# Revit family: QF_BOURGEAT_plaque_chauffante_classic_inox_600x400
name_source: partatom
category: Equipement spécialisé
revit_build: Autodesk Revit 2015 (Build: 20140606_1530(x64)
units: mm (PartAtom-declared; Revit-internal decimal feet)

## types (2) — shared parameters
Charge max = 10.00 kg
Fabricant = BOURGEAT
Fréquence = 50 Hz
Indice de protection = 21
Longueur hors tout = 600 mm
Phase = 2
Poids net à vide = 18.00 kg
Profondeur hors tout = 400 mm  [stored 1.31234 ft]
Spécification du Fabricant = PLAQUE CHAUFFANTE
Tension = 230 V
URL catalogue = http://www.bourgeat.fr

## per-type parameters (varying)
| type | Hauteur hors tout | Intensité nominale | Modèle | Puissance électrique  | lampe_IR |
| plaque_classic_inox | 90 mm  [stored 0.295276 ft] | 2 A | 870904 | 500 W | Non |
| plaque_classic_inox+lampe_IR | 500 mm  [stored 1.64042 ft] | 5 A | 870904+870990 | 1100 W | Oui |

note: [stored X ft] marks values corroborated as IEEE doubles in the binary element streams (Revit-internal decimal feet)
